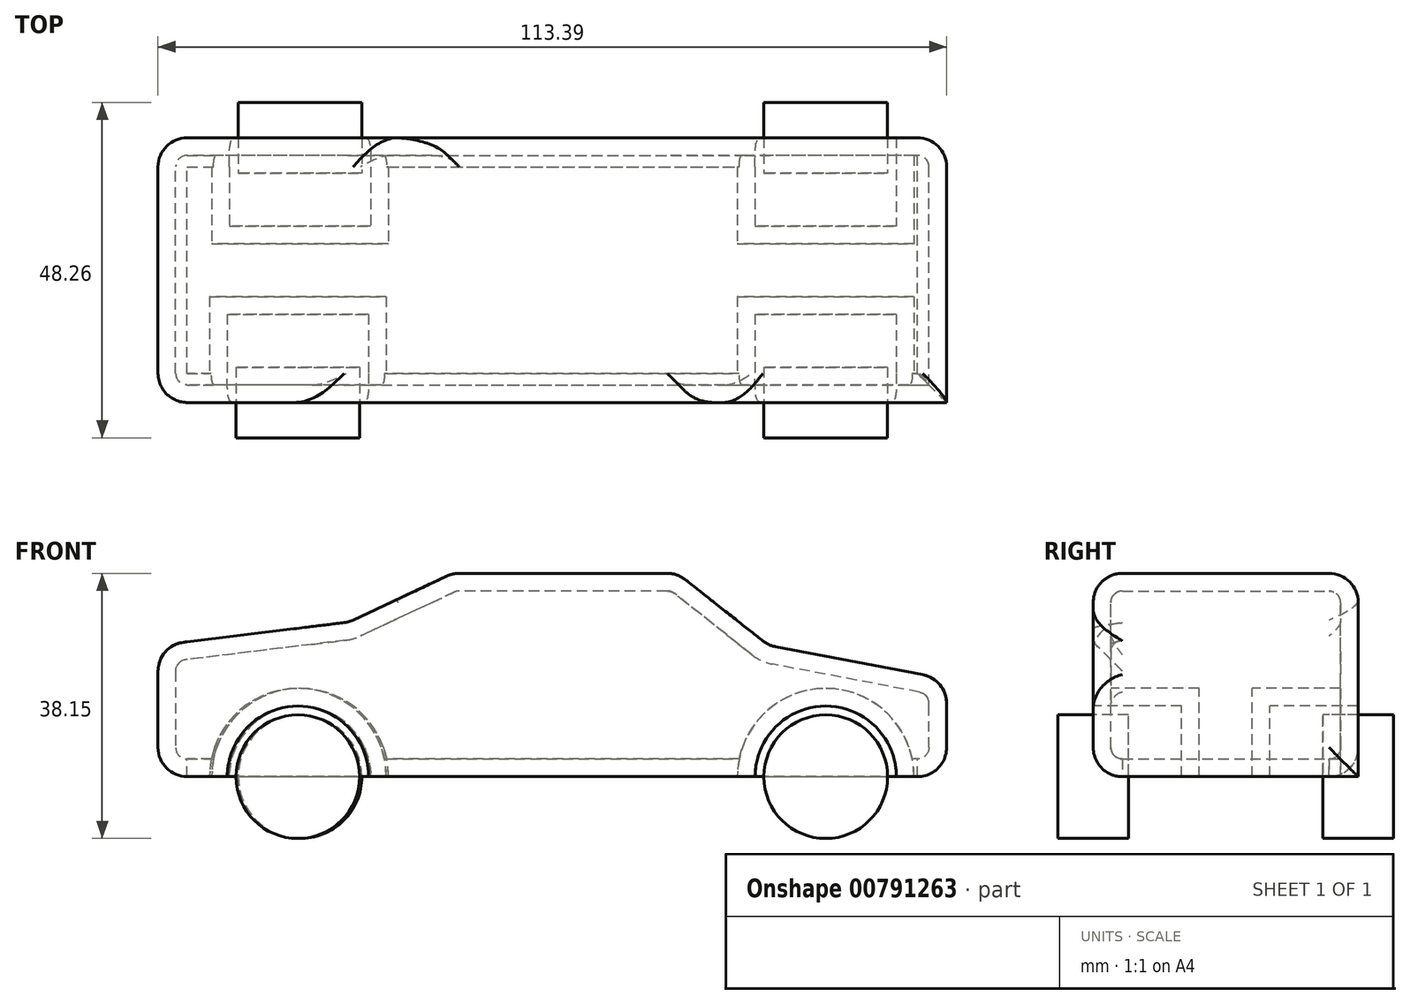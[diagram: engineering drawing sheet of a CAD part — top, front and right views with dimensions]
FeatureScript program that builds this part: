
annotation { "Feature Type Name" : "Feature", "Feature Type Description" : "" }
export const myFeature = defineFeature(function(context is Context, id is Id, definition is map)
    precondition{}
    {
        {
            var Q0;
            Q0=qCreatedBy(makeId("Front.planeOp"),FACE);
            var sketch = newSketch(context, id + "F0", { "sketchPlane" : qUnion([Q0])});
            skLineSegment(sketch, "E0", {"start": v(61.42, 0) * mm, "end": v(61.42, 14.02) * mm});
            skLineSegment(sketch, "E1", {"start": v(61.42, 14.02) * mm, "end": v(35.81, 18.9) * mm});
            skLineSegment(sketch, "E2", {"start": v(35.81, 18.9) * mm, "end": v(22.7, 29.26) * mm});
            skLineSegment(sketch, "E3", {"start": v(22.7, 29.26) * mm, "end": v(-9.6, 29.26) * mm});
            skLineSegment(sketch, "E4", {"start": v(-9.6, 29.26) * mm, "end": v(-24.54, 22.25) * mm});
            skLineSegment(sketch, "E5", {"start": v(-24.54, 22.25) * mm, "end": v(-51.97, 18.9) * mm});
            skLineSegment(sketch, "E6", {"start": v(-51.97, 18.9) * mm, "end": v(-51.97, 4.57) * mm});
            skLineSegment(sketch, "E7", {"start": v(-51.97, 4.57) * mm, "end": v(-51.97, 0) * mm});
            skLineSegment(sketch, "E8", {"start": v(-51.97, 0) * mm, "end": v(61.42, 0) * mm});
            skSolve(sketch);
        }
        {
            var Q0;
            Q0 = qSketchRegion(id + "F0", true);
            extrude(context, id + "F1", {"entities" : qUnion([Q0]), "endBound" : BoundingType.SYMMETRIC, "depth" : 38.1 * mm, "offsetDistance" : 25.4 * mm});
        }
        {
            var Q0;
            Q0=makeQuery(id+"F1.opExtrude","CAP_FACE",FACE,{"disambiguationData":[OSD([sQuery(id+"F0.wireOp",EDGE,"E0"),sQuery(id+"F0.wireOp",EDGE,"E1"),sQuery(id+"F0.wireOp",EDGE,"E2"),sQuery(id+"F0.wireOp",EDGE,"E3"),sQuery(id+"F0.wireOp",EDGE,"E4"),sQuery(id+"F0.wireOp",EDGE,"E5"),sQuery(id+"F0.wireOp",EDGE,"E6"),sQuery(id+"F0.wireOp",EDGE,"E7"),sQuery(id+"F0.wireOp",EDGE,"E8")])],"isStart":true});
            var sketch = newSketch(context, id + "F2", { "sketchPlane" : qUnion([Q0])});
            skCircle(sketch, "E9", {"center": v(-44.04, 0) * mm, "radius": 10.16 * mm});
            skCircle(sketch, "E10", {"center": v(31.55, 0) * mm, "radius": 10.16 * mm});
            skSolve(sketch);
        }
        {
            var Q0;
            Q0=makeQuery(id+"F1.opExtrude","CAP_FACE",FACE,{"disambiguationData":[OSD([sQuery(id+"F0.wireOp",EDGE,"E0"),sQuery(id+"F0.wireOp",EDGE,"E1"),sQuery(id+"F0.wireOp",EDGE,"E2"),sQuery(id+"F0.wireOp",EDGE,"E3"),sQuery(id+"F0.wireOp",EDGE,"E4"),sQuery(id+"F0.wireOp",EDGE,"E5"),sQuery(id+"F0.wireOp",EDGE,"E6"),sQuery(id+"F0.wireOp",EDGE,"E7"),sQuery(id+"F0.wireOp",EDGE,"E8")])],"isStart":false});
            var sketch = newSketch(context, id + "F3", { "sketchPlane" : qUnion([Q0])});
            skCircle(sketch, "E11", {"center": v(-31.85, 0) * mm, "radius": 10.16 * mm});
            skCircle(sketch, "E12", {"center": v(44.04, 0) * mm, "radius": 10.16 * mm});
            skSolve(sketch);
        }
        {
            var Q0;
            {var subQ0=sQuery(id+"F3.wireOp",EDGE,"E11");var subQ1=makeQuery(id+"F1.opExtrude","CAP_EDGE",EDGE,{"disambiguationData":[OSD([sQuery(id+"F0.wireOp",EDGE,"E8")])],"isStart":false});var subQ2=makeQuery(id+"F3.imprint","INTERSECT",VERTEX,{"disambiguationData":[OD(0.0)],"derivedFrom":[subQ1,subQ0]});Q0=makeQuery(id+"F3.imprint","IMPRINT",FACE,{"disambiguationData":[TD([[makeQuery(id+"F3.imprint","IMPRINT",EDGE,{"disambiguationData":[TD([[subQ2,1.0]])],"derivedFrom":subQ0}),1.0]])]});}
            var Q1;
            {var subQ0=sQuery(id+"F2.wireOp",EDGE,"E10");var subQ1=makeQuery(id+"F1.opExtrude","CAP_EDGE",EDGE,{"disambiguationData":[OSD([sQuery(id+"F0.wireOp",EDGE,"E8")])],"isStart":true});var subQ2=makeQuery(id+"F2.imprint","INTERSECT",VERTEX,{"disambiguationData":[OD(0.0)],"derivedFrom":[subQ1,subQ0]});Q1=makeQuery(id+"F2.imprint","IMPRINT",FACE,{"disambiguationData":[TD([[makeQuery(id+"F2.imprint","IMPRINT",EDGE,{"disambiguationData":[TD([[subQ2,-1.0]])],"derivedFrom":subQ0}),1.0]])]});}
            var Q2;
            {var subQ0=sQuery(id+"F2.wireOp",EDGE,"E9");var subQ1=makeQuery(id+"F1.opExtrude","CAP_EDGE",EDGE,{"disambiguationData":[OSD([sQuery(id+"F0.wireOp",EDGE,"E8")])],"isStart":true});var subQ2=makeQuery(id+"F2.imprint","INTERSECT",VERTEX,{"disambiguationData":[OD(0.0)],"derivedFrom":[subQ1,subQ0]});Q2=makeQuery(id+"F2.imprint","IMPRINT",FACE,{"disambiguationData":[TD([[makeQuery(id+"F2.imprint","IMPRINT",EDGE,{"disambiguationData":[TD([[subQ2,1.0]])],"derivedFrom":subQ0}),1.0]])]});}
            var Q3;
            {var subQ0=sQuery(id+"F3.wireOp",EDGE,"E12");var subQ1=makeQuery(id+"F1.opExtrude","CAP_EDGE",EDGE,{"disambiguationData":[OSD([sQuery(id+"F0.wireOp",EDGE,"E8")])],"isStart":false});var subQ2=makeQuery(id+"F3.imprint","INTERSECT",VERTEX,{"disambiguationData":[OD(0.0)],"derivedFrom":[subQ1,subQ0]});Q3=makeQuery(id+"F3.imprint","IMPRINT",FACE,{"disambiguationData":[TD([[makeQuery(id+"F3.imprint","IMPRINT",EDGE,{"disambiguationData":[TD([[subQ2,-1.0]])],"derivedFrom":subQ0}),1.0]])]});}
            var Q4;
            {var subQ0=sQuery(id+"F3.wireOp",EDGE,"E12");var subQ1=makeQuery(id+"F1.opExtrude","CAP_EDGE",EDGE,{"disambiguationData":[OSD([sQuery(id+"F0.wireOp",EDGE,"E8")])],"isStart":false});var subQ2=makeQuery(id+"F3.imprint","INTERSECT",VERTEX,{"disambiguationData":[OD(0.0)],"derivedFrom":[subQ1,subQ0]});Q4=makeQuery(id+"F3.imprint","IMPRINT",FACE,{"disambiguationData":[TD([[makeQuery(id+"F3.imprint","IMPRINT",EDGE,{"disambiguationData":[TD([[subQ2,1.0]])],"derivedFrom":subQ0}),1.0]])]});}
            var Q5;
            {var subQ0=sQuery(id+"F2.wireOp",EDGE,"E9");var subQ1=makeQuery(id+"F1.opExtrude","CAP_EDGE",EDGE,{"disambiguationData":[OSD([sQuery(id+"F0.wireOp",EDGE,"E8")])],"isStart":true});var subQ2=makeQuery(id+"F2.imprint","INTERSECT",VERTEX,{"disambiguationData":[OD(0.0)],"derivedFrom":[subQ1,subQ0]});Q5=makeQuery(id+"F2.imprint","IMPRINT",FACE,{"disambiguationData":[TD([[makeQuery(id+"F2.imprint","IMPRINT",EDGE,{"disambiguationData":[TD([[subQ2,-1.0]])],"derivedFrom":subQ0}),1.0]])]});}
            var Q6;
            {var subQ0=sQuery(id+"F3.wireOp",EDGE,"E11");var subQ1=makeQuery(id+"F1.opExtrude","CAP_EDGE",EDGE,{"disambiguationData":[OSD([sQuery(id+"F0.wireOp",EDGE,"E8")])],"isStart":false});var subQ2=makeQuery(id+"F3.imprint","INTERSECT",VERTEX,{"disambiguationData":[OD(0.0)],"derivedFrom":[subQ1,subQ0]});Q6=makeQuery(id+"F3.imprint","IMPRINT",FACE,{"disambiguationData":[TD([[makeQuery(id+"F3.imprint","IMPRINT",EDGE,{"disambiguationData":[TD([[subQ2,-1.0]])],"derivedFrom":subQ0}),1.0]])]});}
            var Q7;
            {var subQ0=sQuery(id+"F2.wireOp",EDGE,"E10");var subQ1=makeQuery(id+"F1.opExtrude","CAP_EDGE",EDGE,{"disambiguationData":[OSD([sQuery(id+"F0.wireOp",EDGE,"E8")])],"isStart":true});var subQ2=makeQuery(id+"F2.imprint","INTERSECT",VERTEX,{"disambiguationData":[OD(0.0)],"derivedFrom":[subQ1,subQ0]});Q7=makeQuery(id+"F2.imprint","IMPRINT",FACE,{"disambiguationData":[TD([[makeQuery(id+"F2.imprint","IMPRINT",EDGE,{"disambiguationData":[TD([[subQ2,1.0]])],"derivedFrom":subQ0}),1.0]])]});}
            extrude(context, id + "F4", {"entities" : qUnion([Q0, Q1, Q2, Q3, Q4, Q5, Q6, Q7]), "operationType" : NewBodyOperationType.REMOVE, "endBound" : BoundingType.SYMMETRIC, "oppositeDirection" : true, "depth" : 25.4 * mm, "offsetDistance" : 25.4 * mm});
        }
        {
            var Q0;
            Q0=makeQuery(id+"F1.opExtrude","CAP_FACE",FACE,{"disambiguationData":[OSD([sQuery(id+"F0.wireOp",EDGE,"E0"),sQuery(id+"F0.wireOp",EDGE,"E1"),sQuery(id+"F0.wireOp",EDGE,"E2"),sQuery(id+"F0.wireOp",EDGE,"E3"),sQuery(id+"F0.wireOp",EDGE,"E4"),sQuery(id+"F0.wireOp",EDGE,"E5"),sQuery(id+"F0.wireOp",EDGE,"E6"),sQuery(id+"F0.wireOp",EDGE,"E7"),sQuery(id+"F0.wireOp",EDGE,"E8")])],"isStart":false});
            var sketch = newSketch(context, id + "F5", { "sketchPlane" : qUnion([Q0])});
            skCircle(sketch, "E13", {"center": v(-31.85, 0) * mm, "radius": 8.9 * mm});
            skCircle(sketch, "E14", {"center": v(44.04, 0) * mm, "radius": 8.9 * mm});
            skSolve(sketch);
        }
        {
            var Q0;
            Q0=makeQuery(id+"F1.opExtrude","CAP_FACE",FACE,{"disambiguationData":[OSD([sQuery(id+"F0.wireOp",EDGE,"E0"),sQuery(id+"F0.wireOp",EDGE,"E1"),sQuery(id+"F0.wireOp",EDGE,"E2"),sQuery(id+"F0.wireOp",EDGE,"E3"),sQuery(id+"F0.wireOp",EDGE,"E4"),sQuery(id+"F0.wireOp",EDGE,"E5"),sQuery(id+"F0.wireOp",EDGE,"E6"),sQuery(id+"F0.wireOp",EDGE,"E7"),sQuery(id+"F0.wireOp",EDGE,"E8")])],"isStart":true});
            var sketch = newSketch(context, id + "F6", { "sketchPlane" : qUnion([Q0])});
            skCircle(sketch, "E15", {"center": v(-44.04, 0) * mm, "radius": 8.9 * mm});
            skCircle(sketch, "E16", {"center": v(31.55, 0) * mm, "radius": 8.9 * mm});
            skSolve(sketch);
        }
        {
            var Q0;
            Q0=makeQuery(id+"F6.imprint","IMPRINT",FACE,{"disambiguationData":[TD([[makeQuery(id+"F6.imprint","IMPRINT",EDGE,{"derivedFrom":sQuery(id+"F6.wireOp",EDGE,"E15")}),1.0]])]});
            var Q1;
            Q1=makeQuery(id+"F5.imprint","IMPRINT",FACE,{"disambiguationData":[TD([[makeQuery(id+"F5.imprint","IMPRINT",EDGE,{"derivedFrom":sQuery(id+"F5.wireOp",EDGE,"E14")}),1.0]])]});
            var Q2;
            Q2=makeQuery(id+"F6.imprint","IMPRINT",FACE,{"disambiguationData":[TD([[makeQuery(id+"F6.imprint","IMPRINT",EDGE,{"derivedFrom":sQuery(id+"F6.wireOp",EDGE,"E16")}),1.0]])]});
            var Q3;
            Q3=makeQuery(id+"F5.imprint","IMPRINT",FACE,{"disambiguationData":[TD([[makeQuery(id+"F5.imprint","IMPRINT",EDGE,{"derivedFrom":sQuery(id+"F5.wireOp",EDGE,"E13")}),1.0]])]});
            extrude(context, id + "F7", {"entities" : qUnion([Q0, Q1, Q2, Q3]), "endBound" : BoundingType.SYMMETRIC, "depth" : 10.16 * mm, "offsetDistance" : 25.4 * mm});
        }
        {
            var Q0;
            Q0=makeQuery(id+"F1.opExtrude","CAP_EDGE",EDGE,{"disambiguationData":[OSD([sQuery(id+"F0.wireOp",EDGE,"E3")])],"isStart":false});
            var Q1;
            Q1=makeQuery(id+"F1.opExtrude","SWEPT_EDGE",EDGE,{"disambiguationData":[OSD([sQuery(id+"F0.wireOp",EDGE,"E3"),sQuery(id+"F0.wireOp",EDGE,"E4")])]});
            var Q2;
            Q2=makeQuery(id+"F1.opExtrude","CAP_EDGE",EDGE,{"disambiguationData":[OSD([sQuery(id+"F0.wireOp",EDGE,"E4")])],"isStart":false});
            var Q3;
            Q3=makeQuery(id+"F1.opExtrude","SWEPT_EDGE",EDGE,{"disambiguationData":[OSD([sQuery(id+"F0.wireOp",EDGE,"E4"),sQuery(id+"F0.wireOp",EDGE,"E5")])]});
            var Q4;
            Q4=makeQuery(id+"F1.opExtrude","SWEPT_EDGE",EDGE,{"disambiguationData":[OSD([sQuery(id+"F0.wireOp",EDGE,"E5"),sQuery(id+"F0.wireOp",EDGE,"E6")])]});
            var Q5;
            Q5=makeQuery(id+"F1.opExtrude","CAP_EDGE",EDGE,{"disambiguationData":[OSD([sQuery(id+"F0.wireOp",EDGE,"E5")])],"isStart":true});
            var Q6;
            Q6=makeQuery(id+"F1.opExtrude","SWEPT_EDGE",EDGE,{"disambiguationData":[OSD([sQuery(id+"F0.wireOp",EDGE,"E2"),sQuery(id+"F0.wireOp",EDGE,"E3")])]});
            var Q7;
            Q7=makeQuery(id+"F1.opExtrude","CAP_EDGE",EDGE,{"disambiguationData":[OSD([sQuery(id+"F0.wireOp",EDGE,"E3")])],"isStart":true});
            var Q8;
            Q8=makeQuery(id+"F1.opExtrude","CAP_EDGE",EDGE,{"disambiguationData":[OSD([sQuery(id+"F0.wireOp",EDGE,"E2")])],"isStart":true});
            var Q9;
            Q9=makeQuery(id+"F1.opExtrude","CAP_EDGE",EDGE,{"disambiguationData":[OSD([sQuery(id+"F0.wireOp",EDGE,"E1")])],"isStart":true});
            var Q10;
            Q10=makeQuery(id+"F1.opExtrude","SWEPT_EDGE",EDGE,{"disambiguationData":[OSD([sQuery(id+"F0.wireOp",EDGE,"E0"),sQuery(id+"F0.wireOp",EDGE,"E1")])]});
            var Q11;
            Q11=makeQuery(id+"F1.opExtrude","CAP_EDGE",EDGE,{"disambiguationData":[OSD([sQuery(id+"F0.wireOp",EDGE,"E1")])],"isStart":false});
            var Q12;
            Q12=makeQuery(id+"F1.opExtrude","SWEPT_EDGE",EDGE,{"disambiguationData":[OSD([sQuery(id+"F0.wireOp",EDGE,"E1"),sQuery(id+"F0.wireOp",EDGE,"E2")])]});
            var Q13;
            {var subQ0=sQuery(id+"F0.wireOp",EDGE,"E8");Q13=makeQuery(id+"F4.boolean.opBoolean","SPLIT",EDGE,{"disambiguationData":[TD([makeQuery(id+"F1.opExtrude","CAP_FACE",FACE,{"disambiguationData":[OSD([sQuery(id+"F0.wireOp",EDGE,"E0"),sQuery(id+"F0.wireOp",EDGE,"E1"),sQuery(id+"F0.wireOp",EDGE,"E2"),sQuery(id+"F0.wireOp",EDGE,"E3"),sQuery(id+"F0.wireOp",EDGE,"E4"),sQuery(id+"F0.wireOp",EDGE,"E5"),sQuery(id+"F0.wireOp",EDGE,"E6"),sQuery(id+"F0.wireOp",EDGE,"E7"),subQ0])],"isStart":false}),makeQuery(id+"F1.opExtrude","SWEPT_FACE",FACE,{"disambiguationData":[OSD([subQ0])]}),makeQuery(id+"F4.opExtrude","SWEPT_FACE",FACE,{"disambiguationData":[OSD([sQuery(id+"F3.wireOp",EDGE,"E11")])]}),makeQuery(id+"F4.opExtrude","SWEPT_FACE",FACE,{"disambiguationData":[OSD([sQuery(id+"F3.wireOp",EDGE,"E12")])]})])],"derivedFrom":makeQuery(id+"F1.opExtrude","CAP_EDGE",EDGE,{"disambiguationData":[OSD([subQ0])],"isStart":false})});}
            var Q14;
            Q14=makeQuery(id+"F1.opExtrude","SWEPT_EDGE",EDGE,{"disambiguationData":[OSD([sQuery(id+"F0.wireOp",EDGE,"E0"),sQuery(id+"F0.wireOp",EDGE,"E8")])]});
            var Q15;
            {var subQ0=sQuery(id+"F0.wireOp",EDGE,"E0");var subQ1=sQuery(id+"F0.wireOp",EDGE,"E8");Q15=makeQuery(id+"F4.boolean.opBoolean","SPLIT",EDGE,{"disambiguationData":[TD([makeQuery(id+"F1.opExtrude","SWEPT_FACE",FACE,{"disambiguationData":[OSD([subQ0])]}),makeQuery(id+"F1.opExtrude","CAP_FACE",FACE,{"disambiguationData":[OSD([subQ0,sQuery(id+"F0.wireOp",EDGE,"E1"),sQuery(id+"F0.wireOp",EDGE,"E2"),sQuery(id+"F0.wireOp",EDGE,"E3"),sQuery(id+"F0.wireOp",EDGE,"E4"),sQuery(id+"F0.wireOp",EDGE,"E5"),sQuery(id+"F0.wireOp",EDGE,"E6"),sQuery(id+"F0.wireOp",EDGE,"E7"),subQ1])],"isStart":false}),makeQuery(id+"F1.opExtrude","SWEPT_FACE",FACE,{"disambiguationData":[OSD([subQ1])]}),makeQuery(id+"F4.opExtrude","SWEPT_FACE",FACE,{"disambiguationData":[OSD([sQuery(id+"F3.wireOp",EDGE,"E12")])]})])],"derivedFrom":makeQuery(id+"F1.opExtrude","CAP_EDGE",EDGE,{"disambiguationData":[OSD([subQ1])],"isStart":false})});}
            var Q16;
            {var subQ0=sQuery(id+"F0.wireOp",EDGE,"E8");var subQ1=sQuery(id+"F0.wireOp",EDGE,"E7");var subQ2=sQuery(id+"F0.wireOp",EDGE,"E6");Q16=makeQuery(id+"F4.boolean.opBoolean","SPLIT",EDGE,{"disambiguationData":[TD([makeQuery(id+"F1.opExtrude","CAP_FACE",FACE,{"disambiguationData":[OSD([sQuery(id+"F0.wireOp",EDGE,"E0"),sQuery(id+"F0.wireOp",EDGE,"E1"),sQuery(id+"F0.wireOp",EDGE,"E2"),sQuery(id+"F0.wireOp",EDGE,"E3"),sQuery(id+"F0.wireOp",EDGE,"E4"),sQuery(id+"F0.wireOp",EDGE,"E5"),subQ2,subQ1,subQ0])],"isStart":false}),makeQuery(id+"F1.opExtrude","SWEPT_FACE",FACE,{"disambiguationData":[OSD([subQ2,subQ1])]}),makeQuery(id+"F1.opExtrude","SWEPT_FACE",FACE,{"disambiguationData":[OSD([subQ0])]}),makeQuery(id+"F4.opExtrude","SWEPT_FACE",FACE,{"disambiguationData":[OSD([sQuery(id+"F3.wireOp",EDGE,"E11")])]})])],"derivedFrom":makeQuery(id+"F1.opExtrude","CAP_EDGE",EDGE,{"disambiguationData":[OSD([subQ0])],"isStart":false})});}
            var Q17;
            Q17=makeQuery(id+"F1.opExtrude","CAP_EDGE",EDGE,{"disambiguationData":[OSD([sQuery(id+"F0.wireOp",EDGE,"E6"),sQuery(id+"F0.wireOp",EDGE,"E7")])],"isStart":true});
            var Q18;
            Q18=makeQuery(id+"F1.opExtrude","SWEPT_EDGE",EDGE,{"disambiguationData":[OSD([sQuery(id+"F0.wireOp",EDGE,"E7"),sQuery(id+"F0.wireOp",EDGE,"E8")])]});
            var Q19;
            Q19=makeQuery(id+"F1.opExtrude","CAP_EDGE",EDGE,{"disambiguationData":[OSD([sQuery(id+"F0.wireOp",EDGE,"E6"),sQuery(id+"F0.wireOp",EDGE,"E7")])],"isStart":false});
            var Q20;
            {var subQ0=sQuery(id+"F0.wireOp",EDGE,"E8");Q20=makeQuery(id+"F4.boolean.opBoolean","SPLIT",EDGE,{"disambiguationData":[TD([makeQuery(id+"F1.opExtrude","CAP_FACE",FACE,{"disambiguationData":[OSD([sQuery(id+"F0.wireOp",EDGE,"E0"),sQuery(id+"F0.wireOp",EDGE,"E1"),sQuery(id+"F0.wireOp",EDGE,"E2"),sQuery(id+"F0.wireOp",EDGE,"E3"),sQuery(id+"F0.wireOp",EDGE,"E4"),sQuery(id+"F0.wireOp",EDGE,"E5"),sQuery(id+"F0.wireOp",EDGE,"E6"),sQuery(id+"F0.wireOp",EDGE,"E7"),subQ0])],"isStart":true}),makeQuery(id+"F1.opExtrude","SWEPT_FACE",FACE,{"disambiguationData":[OSD([subQ0])]}),makeQuery(id+"F4.opExtrude","SWEPT_FACE",FACE,{"disambiguationData":[OSD([sQuery(id+"F2.wireOp",EDGE,"E9")])]}),makeQuery(id+"F4.opExtrude","SWEPT_FACE",FACE,{"disambiguationData":[OSD([sQuery(id+"F2.wireOp",EDGE,"E10")])]})])],"derivedFrom":makeQuery(id+"F1.opExtrude","CAP_EDGE",EDGE,{"disambiguationData":[OSD([subQ0])],"isStart":true})});}
            var Q21;
            {var subQ0=sQuery(id+"F0.wireOp",EDGE,"E8");var subQ1=sQuery(id+"F0.wireOp",EDGE,"E7");var subQ2=sQuery(id+"F0.wireOp",EDGE,"E6");Q21=makeQuery(id+"F4.boolean.opBoolean","SPLIT",EDGE,{"disambiguationData":[TD([makeQuery(id+"F1.opExtrude","CAP_FACE",FACE,{"disambiguationData":[OSD([sQuery(id+"F0.wireOp",EDGE,"E0"),sQuery(id+"F0.wireOp",EDGE,"E1"),sQuery(id+"F0.wireOp",EDGE,"E2"),sQuery(id+"F0.wireOp",EDGE,"E3"),sQuery(id+"F0.wireOp",EDGE,"E4"),sQuery(id+"F0.wireOp",EDGE,"E5"),subQ2,subQ1,subQ0])],"isStart":true}),makeQuery(id+"F1.opExtrude","SWEPT_FACE",FACE,{"disambiguationData":[OSD([subQ2,subQ1])]}),makeQuery(id+"F1.opExtrude","SWEPT_FACE",FACE,{"disambiguationData":[OSD([subQ0])]}),makeQuery(id+"F4.opExtrude","SWEPT_FACE",FACE,{"disambiguationData":[OSD([sQuery(id+"F2.wireOp",EDGE,"E10")])]})])],"derivedFrom":makeQuery(id+"F1.opExtrude","CAP_EDGE",EDGE,{"disambiguationData":[OSD([subQ0])],"isStart":true})});}
            var Q22;
            Q22=makeQuery(id+"F1.opExtrude","CAP_EDGE",EDGE,{"disambiguationData":[OSD([sQuery(id+"F0.wireOp",EDGE,"E0")])],"isStart":true});
            fillet(context, id + "F8", {"entities" : qUnion([Q0, Q1, Q2, Q3, Q4, Q5, Q6, Q7, Q8, Q9, Q10, Q11, Q12, Q13, Q14, Q15, Q16, Q17, Q18, Q19, Q20, Q21, Q22]), "radius" : 4.2 * mm, "tangentPropagation" : true, "allowEdgeOverflow" : false});
        }
        {
            var Q0;
            Q0=makeQuery(id+"F1.opExtrude","SWEPT_FACE",FACE,{"disambiguationData":[OSD([sQuery(id+"F0.wireOp",EDGE,"E8")])]});
            shell(context, id + "F9", {"entities" : qUnion([Q0]), "thickness" : 2.54 * mm});
        }
    });
